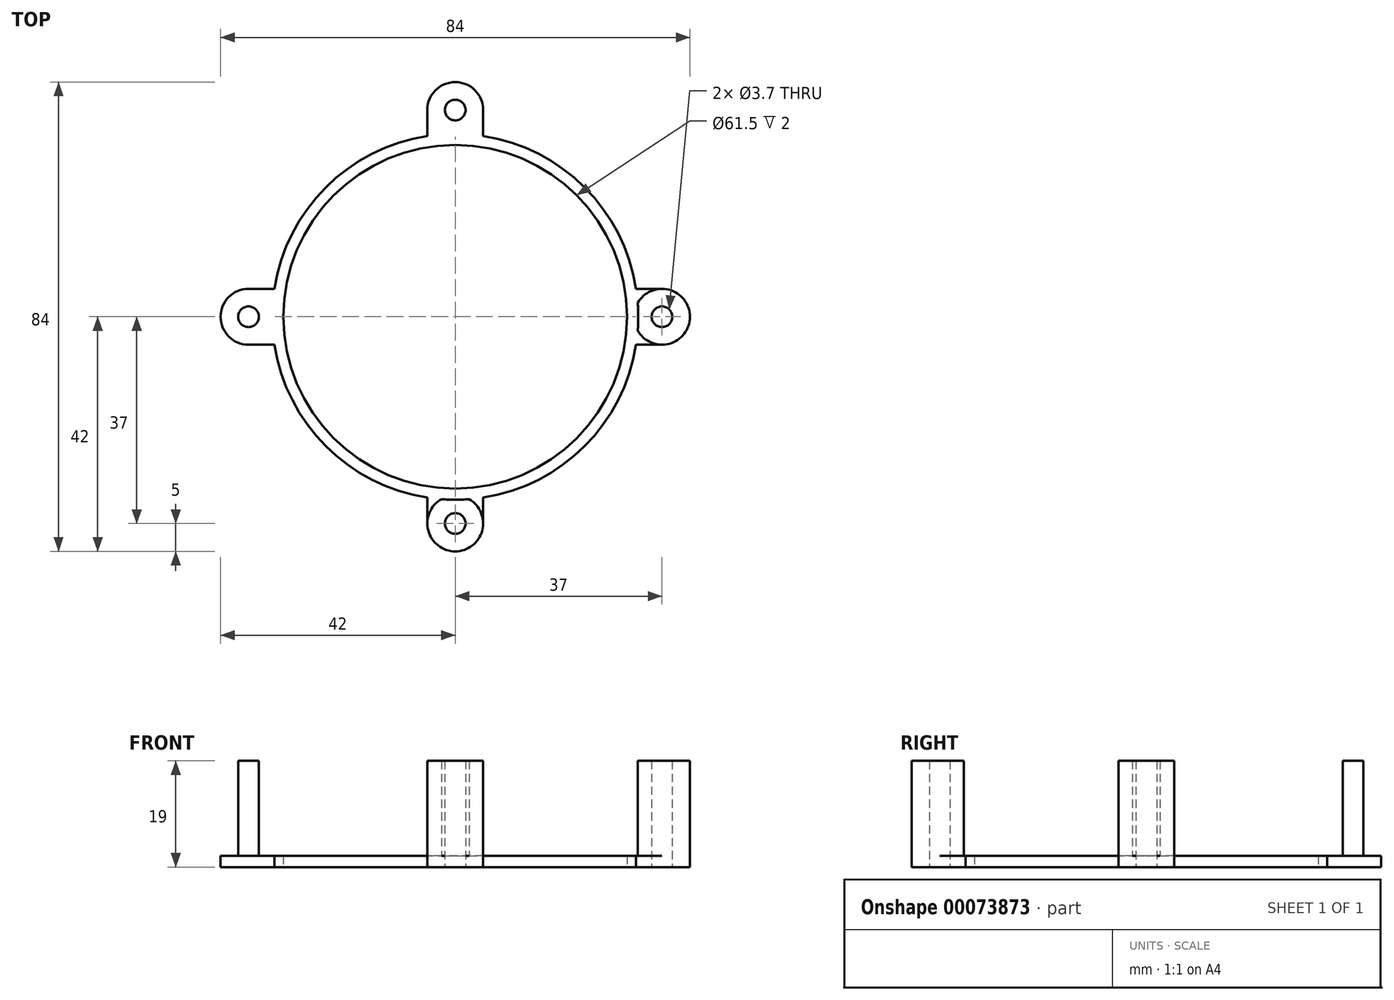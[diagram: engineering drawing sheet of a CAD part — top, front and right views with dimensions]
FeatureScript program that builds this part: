
annotation { "Feature Type Name" : "Feature", "Feature Type Description" : "" }
export const myFeature = defineFeature(function(context is Context, id is Id, definition is map)
    precondition{}
    {
        {
            var Q0;
            Q0=qCreatedBy(makeId("Top.planeOp"),FACE);
            var sketch = newSketch(context, id + "F0", { "sketchPlane" : qUnion([Q0])});
            skCircle(sketch, "E0", {"center": v(0, 0) * mm, "radius": 32.75 * mm});
            skCircle(sketch, "E1", {"center": v(0, 0) * mm, "radius": 30.75 * mm});
            skCircle(sketch, "E2", {"center": v(0, 37) * mm, "radius": 5 * mm});
            skLineSegment(sketch, "E3", {"start": v(-5, 37) * mm, "end": v(-5, 32.37) * mm});
            skLineSegment(sketch, "E4", {"start": v(5, 37) * mm, "end": v(5, 32.37) * mm});
            skCircle(sketch, "E5", {"center": v(0, 37) * mm, "radius": 1.85 * mm});
            skLineSegment(sketch, "E6.MirrorCS", {"start": v(-5, -37) * mm, "end": v(-5, -32.37) * mm});
            skCircle(sketch, "E7.MirrorC", {"center": v(0, -37) * mm, "radius": 1.85 * mm});
            skLineSegment(sketch, "E8.MirrorCS", {"start": v(5, -37) * mm, "end": v(5, -32.37) * mm});
            skCircle(sketch, "E9.MirrorC", {"center": v(0, -37) * mm, "radius": 5 * mm});
            skCircle(sketch, "E10", {"center": v(-37, 0) * mm, "radius": 5 * mm});
            skCircle(sketch, "E11", {"center": v(-37, 0) * mm, "radius": 1.85 * mm});
            skLineSegment(sketch, "E12", {"start": v(-37, 5) * mm, "end": v(-32.37, 5) * mm});
            skLineSegment(sketch, "E13", {"start": v(-37, -5) * mm, "end": v(-32.37, -5) * mm});
            skLineSegment(sketch, "E14.MirrorCS", {"start": v(37, 5) * mm, "end": v(32.37, 5) * mm});
            skCircle(sketch, "E15.MirrorC", {"center": v(37, 0) * mm, "radius": 1.85 * mm});
            skLineSegment(sketch, "E16.MirrorCS", {"start": v(37, -5) * mm, "end": v(32.37, -5) * mm});
            skCircle(sketch, "E17.MirrorC", {"center": v(37, 0) * mm, "radius": 5 * mm});
            skSolve(sketch);
        }
        {
            var Q0;
            Q0 = qSketchRegion(id + "F0", true);
            var Q1;
            {var subQ0=sQuery(id+"F0.wireOp",EDGE,"E2");var subQ1=sQuery(id+"F0.wireOp",EDGE,"E0");var subQ2=makeQuery(id+"F0.imprint","INTERSECT",VERTEX,{"disambiguationData":[OD(0.0)],"derivedFrom":[subQ1,subQ0]});Q1=makeQuery(id+"F0.imprint","IMPRINT",FACE,{"disambiguationData":[TD([[makeQuery(id+"F0.imprint","IMPRINT",EDGE,{"disambiguationData":[TD([[subQ2,-1.0]])],"derivedFrom":subQ1}),1.0]])]});}
            var Q2;
            {var subQ0=sQuery(id+"F0.wireOp",EDGE,"E10");var subQ1=sQuery(id+"F0.wireOp",EDGE,"E0");var subQ2=makeQuery(id+"F0.imprint","INTERSECT",VERTEX,{"disambiguationData":[OD(0.0)],"derivedFrom":[subQ1,subQ0]});Q2=makeQuery(id+"F0.imprint","IMPRINT",FACE,{"disambiguationData":[TD([[makeQuery(id+"F0.imprint","IMPRINT",EDGE,{"disambiguationData":[TD([[subQ2,-1.0]])],"derivedFrom":subQ1}),1.0]])]});}
            var Q3;
            {var subQ0=sQuery(id+"F0.wireOp",EDGE,"E9.MirrorC");var subQ1=sQuery(id+"F0.wireOp",EDGE,"E0");var subQ2=makeQuery(id+"F0.imprint","INTERSECT",VERTEX,{"disambiguationData":[OD(0.0)],"derivedFrom":[subQ1,subQ0]});Q3=makeQuery(id+"F0.imprint","IMPRINT",FACE,{"disambiguationData":[TD([[makeQuery(id+"F0.imprint","IMPRINT",EDGE,{"disambiguationData":[TD([[subQ2,-1.0]])],"derivedFrom":subQ1}),1.0]])]});}
            var Q4;
            {var subQ0=sQuery(id+"F0.wireOp",EDGE,"E17.MirrorC");var subQ1=sQuery(id+"F0.wireOp",EDGE,"E0");var subQ2=makeQuery(id+"F0.imprint","INTERSECT",VERTEX,{"disambiguationData":[OD(0.0)],"derivedFrom":[subQ1,subQ0]});Q4=makeQuery(id+"F0.imprint","IMPRINT",FACE,{"disambiguationData":[TD([[makeQuery(id+"F0.imprint","IMPRINT",EDGE,{"disambiguationData":[TD([[subQ2,1.0]])],"derivedFrom":subQ1}),1.0]])]});}
            extrude(context, id + "F1", {"entities" : qUnion([Q0, Q1, Q2, Q3, Q4]), "depth" : 2 * mm});
        }
        {
            var Q0;
            Q0=makeQuery(id+"F0.imprint","IMPRINT",FACE,{"disambiguationData":[TD([[makeQuery(id+"F0.imprint","IMPRINT",EDGE,{"derivedFrom":sQuery(id+"F0.wireOp",EDGE,"E5")}),1.0]])]});
            var Q1;
            Q1=makeQuery(id+"F0.imprint","IMPRINT",FACE,{"disambiguationData":[TD([[makeQuery(id+"F0.imprint","IMPRINT",EDGE,{"derivedFrom":sQuery(id+"F0.wireOp",EDGE,"E11")}),1.0]])]});
            var Q2;
            Q2=makeQuery(id+"F0.imprint","IMPRINT",FACE,{"disambiguationData":[TD([[makeQuery(id+"F0.imprint","IMPRINT",EDGE,{"derivedFrom":sQuery(id+"F0.wireOp",EDGE,"E7.MirrorC")}),-1.0]])]});
            var Q3;
            Q3=makeQuery(id+"F0.imprint","IMPRINT",FACE,{"disambiguationData":[TD([[makeQuery(id+"F0.imprint","IMPRINT",EDGE,{"derivedFrom":sQuery(id+"F0.wireOp",EDGE,"E15.MirrorC")}),-1.0]])]});
            extrude(context, id + "F2", {"entities" : qUnion([Q0, Q1, Q2, Q3]), "operationType" : NewBodyOperationType.ADD, "depth" : 19 * mm});
        }
    });
